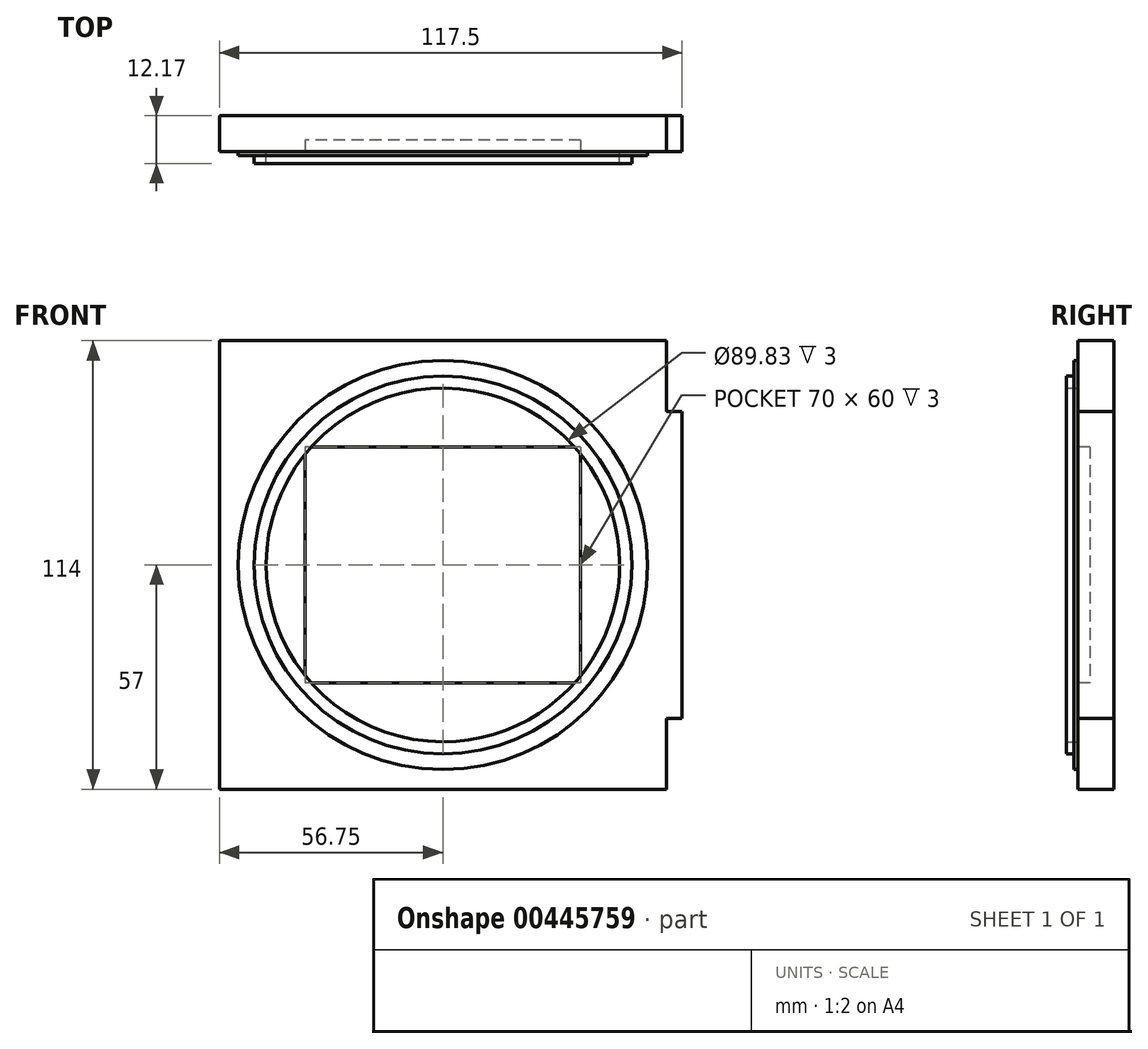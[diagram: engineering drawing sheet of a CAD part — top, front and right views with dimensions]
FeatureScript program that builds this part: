
annotation { "Feature Type Name" : "Feature", "Feature Type Description" : "" }
export const myFeature = defineFeature(function(context is Context, id is Id, definition is map)
    precondition{}
    {
        {
            var Q0;
            Q0=qCreatedBy(makeId("Front.planeOp"),FACE);
            var sketch = newSketch(context, id + "F0", { "sketchPlane" : qUnion([Q0])});
            skLineSegment(sketch, "E0.bottom", {"start": v(56.75, 57) * mm, "end": v(-56.75, 57) * mm});
            skLineSegment(sketch, "E0.top", {"start": v(56.75, -57) * mm, "end": v(-56.75, -57) * mm});
            skLineSegment(sketch, "E0.left", {"start": v(56.75, 57) * mm, "end": v(56.75, -57) * mm});
            skLineSegment(sketch, "E0.right", {"start": v(-56.75, 57) * mm, "end": v(-56.75, -57) * mm});
            skPoint(sketch, "E0.middle", {"position": v(0, 0) * mm});
            skLineSegment(sketch, "E1.bottom", {"start": v(56.75, 39) * mm, "end": v(60.75, 39) * mm});
            skLineSegment(sketch, "E1.top", {"start": v(56.75, -39) * mm, "end": v(60.75, -39) * mm});
            skLineSegment(sketch, "E1.left", {"start": v(56.75, 39) * mm, "end": v(56.75, -39) * mm});
            skLineSegment(sketch, "E1.right", {"start": v(60.75, 39) * mm, "end": v(60.75, -39) * mm});
            skSolve(sketch);
        }
        {
            var Q0;
            Q0 = qSketchRegion(id + "F0", true);
            extrude(context, id + "F1", {"entities" : qUnion([Q0]), "depth" : 9.17 * mm});
        }
        {
            var Q0;
            Q0=makeQuery(id+"F1.opExtrude","CAP_FACE",FACE,{"disambiguationData":[OSD([sQuery(id+"F0.wireOp",EDGE,"E0.bottom"),sQuery(id+"F0.wireOp",EDGE,"E0.top"),sQuery(id+"F0.wireOp",EDGE,"E0.left"),sQuery(id+"F0.wireOp",EDGE,"E0.right"),sQuery(id+"F0.wireOp",EDGE,"E1.bottom"),sQuery(id+"F0.wireOp",EDGE,"E1.top"),sQuery(id+"F0.wireOp",EDGE,"E1.right")])],"isStart":false});
            var sketch = newSketch(context, id + "F2", { "sketchPlane" : qUnion([Q0])});
            skCircle(sketch, "E2", {"center": v(0, 0) * mm, "radius": 48 * mm});
            skCircle(sketch, "E3", {"center": v(0, 0) * mm, "radius": 44.92 * mm});
            skSolve(sketch);
        }
        {
            var Q0;
            Q0 = qSketchRegion(id + "F2", true);
            extrude(context, id + "F3", {"entities" : qUnion([Q0]), "operationType" : NewBodyOperationType.ADD, "depth" : 3 * mm});
        }
        {
            var Q0;
            {var subQ0=sQuery(id+"F0.wireOp",EDGE,"E0.left");var subQ1=sQuery(id+"F0.wireOp",EDGE,"E0.bottom");var subQ3=sQuery(id+"F0.wireOp",EDGE,"E1.bottom");var subQ4=sQuery(id+"F0.wireOp",EDGE,"E0.top");var subQ5=sQuery(id+"F0.wireOp",EDGE,"E1.top");var subQ6=sQuery(id+"F0.wireOp",EDGE,"E0.right");var subQ7=sQuery(id+"F0.wireOp",EDGE,"E1.right");Q0=makeQuery(id+"F3.boolean.opBoolean","SPLIT",FACE,{"disambiguationData":[TD([makeQuery(id+"F1.opExtrude","SWEPT_FACE",FACE,{"disambiguationData":[OSD([subQ1])]})])],"derivedFrom":makeQuery(id+"F1.opExtrude","CAP_FACE",FACE,{"disambiguationData":[OSD([subQ1,subQ4,subQ0,subQ6,subQ3,subQ5,subQ7])],"isStart":false})});}
            var sketch = newSketch(context, id + "F4", { "sketchPlane" : qUnion([Q0])});
            skCircle(sketch, "E4", {"center": v(0, 0) * mm, "radius": 52 * mm});
            skCircle(sketch, "E5", {"center": v(0, 0) * mm, "radius": 45.82 * mm});
            skSolve(sketch);
        }
        {
            var Q0;
            Q0 = qSketchRegion(id + "F4", true);
            extrude(context, id + "F5", {"entities" : qUnion([Q0]), "operationType" : NewBodyOperationType.ADD, "depth" : 1 * mm});
        }
        {
            var Q0;
            Q0=makeQuery(id+"F3.boolean.opBoolean","SPLIT",FACE,{"disambiguationData":[TD([makeQuery(id+"F3.opExtrude","SWEPT_FACE",FACE,{"disambiguationData":[OSD([sQuery(id+"F2.wireOp",EDGE,"E3")])]})])],"derivedFrom":makeQuery(id+"F1.opExtrude","CAP_FACE",FACE,{"disambiguationData":[OSD([sQuery(id+"F0.wireOp",EDGE,"E0.bottom"),sQuery(id+"F0.wireOp",EDGE,"E0.top"),sQuery(id+"F0.wireOp",EDGE,"E0.left"),sQuery(id+"F0.wireOp",EDGE,"E0.right"),sQuery(id+"F0.wireOp",EDGE,"E1.bottom"),sQuery(id+"F0.wireOp",EDGE,"E1.top"),sQuery(id+"F0.wireOp",EDGE,"E1.right")])],"isStart":false})});
            var sketch = newSketch(context, id + "F6", { "sketchPlane" : qUnion([Q0])});
            skLineSegment(sketch, "E6.bottom", {"start": v(35, 30) * mm, "end": v(-35, 30) * mm});
            skLineSegment(sketch, "E6.top", {"start": v(35, -30) * mm, "end": v(-35, -30) * mm});
            skLineSegment(sketch, "E6.left", {"start": v(35, 30) * mm, "end": v(35, -30) * mm});
            skLineSegment(sketch, "E6.right", {"start": v(-35, 30) * mm, "end": v(-35, -30) * mm});
            skPoint(sketch, "E6.middle", {"position": v(0, 0) * mm});
            skSolve(sketch);
        }
        {
            var Q0;
            Q0 = qSketchRegion(id + "F6", true);
            extrude(context, id + "F7", {"entities" : qUnion([Q0]), "operationType" : NewBodyOperationType.REMOVE, "oppositeDirection" : true, "depth" : 3 * mm});
        }
    });
